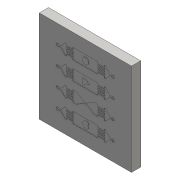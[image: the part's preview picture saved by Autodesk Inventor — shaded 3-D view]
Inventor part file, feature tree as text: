
AUTODESK INVENTOR PART (.ipt)
format: ipt  version: 2016 (Build 200138000, 138)  size: 401,920 bytes
history: native  units: mm
features: sketch x3, extrude x3, other x1
ambient origin geometry x8: Origin, YZ Plane, XZ Plane, XY Plane, X Axis, Y Axis, Z Axis, Center Point
bodies: Body1 (feature_tree), Body2 (feature_tree)
feature tree (7):
  other  "Sólido1"
  sketch  "Boceto1"  dims[d1=5.0mm d2=0.0mm d3=0.2mm d4=0.0mm]
  extrude  "Extrusión1"  Depth=0.2mm TaperAngle=0.0deg
  extrude  "Extrusión2"  Depth=0.7mm
  extrude  "Extrusión3"  Depth=0.2mm
  sketch  "Boceto2"  dims[d5=0.7mm d6=0.7mm]
  sketch  "Boceto3"  dims[d7=0.7mm d8=0.7mm d9=0.7mm d10=0.7mm d11=0.7mm d12=0.7mm d13=0.2mm d14=0.0mm]
